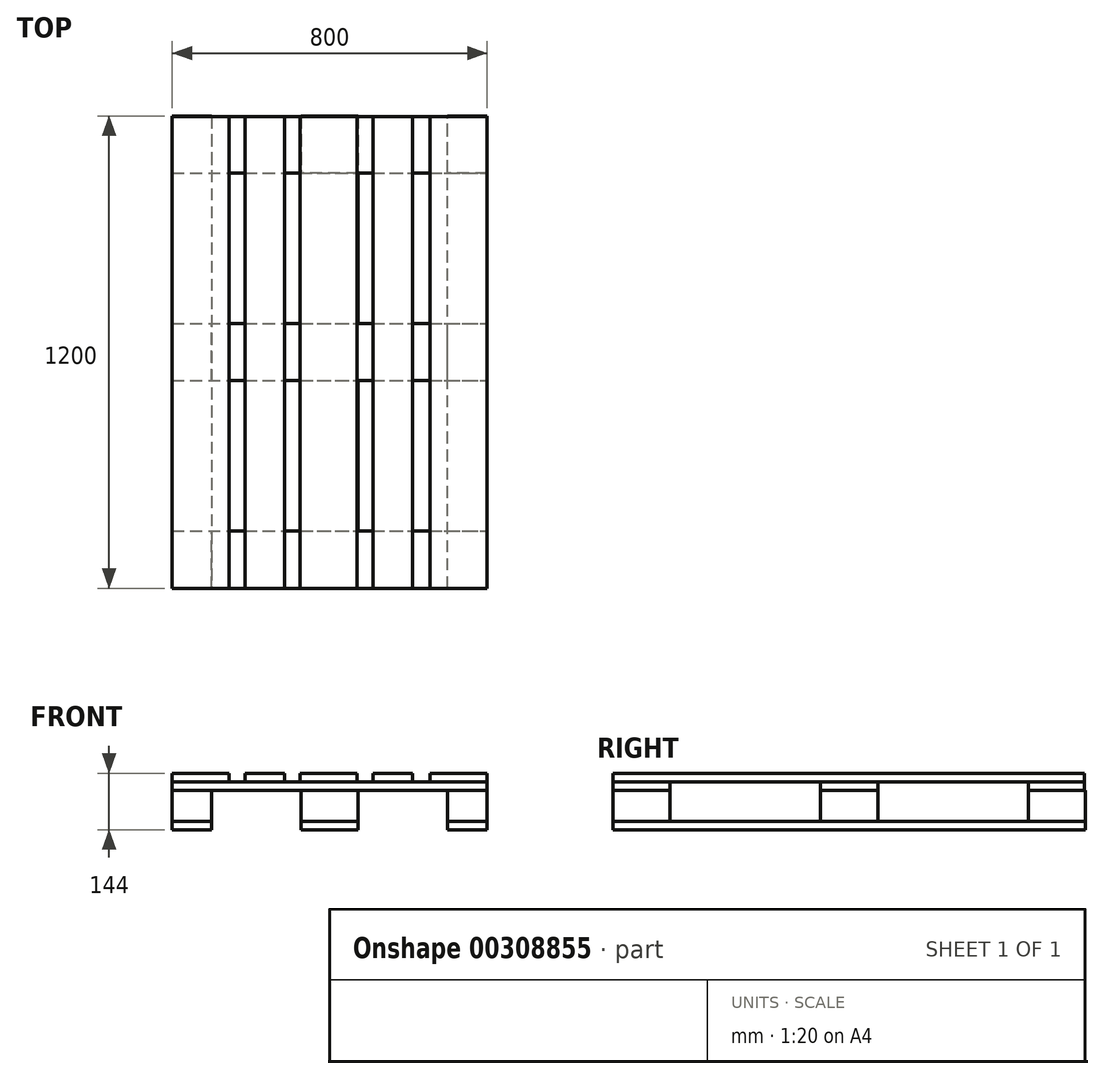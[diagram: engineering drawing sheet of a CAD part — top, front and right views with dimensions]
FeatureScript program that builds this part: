
annotation { "Feature Type Name" : "Feature", "Feature Type Description" : "" }
export const myFeature = defineFeature(function(context is Context, id is Id, definition is map)
    precondition{}
    {
        {
            var Q0;
            Q0=qCreatedBy(makeId("Top.planeOp"),FACE);
            var sketch = newSketch(context, id + "F0", { "sketchPlane" : qUnion([Q0])});
            skLineSegment(sketch, "E0.bottom", {"start": v(-100, 600) * mm, "end": v(0, 600) * mm});
            skLineSegment(sketch, "E0.top", {"start": v(-100, -600) * mm, "end": v(0, -600) * mm});
            skLineSegment(sketch, "E0.left", {"start": v(-100, 600) * mm, "end": v(-100, -600) * mm});
            skLineSegment(sketch, "E0.right", {"start": v(0, 600) * mm, "end": v(0, -600) * mm});
            skLineSegment(sketch, "E1.bottom", {"start": v(227.5, -600) * mm, "end": v(372.5, -600) * mm});
            skLineSegment(sketch, "E1.top", {"start": v(227.5, 600) * mm, "end": v(372.5, 600) * mm});
            skLineSegment(sketch, "E1.left", {"start": v(227.5, -600) * mm, "end": v(227.5, 600) * mm});
            skLineSegment(sketch, "E1.right", {"start": v(372.5, -600) * mm, "end": v(372.5, 600) * mm});
            skPoint(sketch, "E2", {"position": v(300, -600) * mm});
            skLineSegment(sketch, "E3.bottom", {"start": v(600, -600) * mm, "end": v(700, -600) * mm});
            skLineSegment(sketch, "E3.top", {"start": v(600, 600) * mm, "end": v(700, 600) * mm});
            skLineSegment(sketch, "E3.left", {"start": v(600, -600) * mm, "end": v(600, 600) * mm});
            skLineSegment(sketch, "E3.right", {"start": v(700, -600) * mm, "end": v(700, 600) * mm});
            skSolve(sketch);
        }
        {
            var Q0;
            Q0=qSketchRegion(id+"F0",true);
            extrude(context, id + "F1", {"entities" : qUnion([Q0]), "depth" : 22 * mm});
        }
        {
            var Q0;
            Q0=makeQuery(id+"F1.opExtrude","CAP_FACE",FACE,{"disambiguationData":[OSD([sQuery(id+"F0.wireOp",EDGE,"E3.bottom"),sQuery(id+"F0.wireOp",EDGE,"E3.top"),sQuery(id+"F0.wireOp",EDGE,"E3.left"),sQuery(id+"F0.wireOp",EDGE,"E3.right")])],"isStart":false});
            var sketch = newSketch(context, id + "F2", { "sketchPlane" : qUnion([Q0])});
            skLineSegment(sketch, "E4.bottom", {"start": v(-100, -600) * mm, "end": v(0, -600) * mm});
            skLineSegment(sketch, "E4.top", {"start": v(-100, -455) * mm, "end": v(0, -455) * mm});
            skLineSegment(sketch, "E4.left", {"start": v(-100, -600) * mm, "end": v(-100, -455) * mm});
            skLineSegment(sketch, "E4.right", {"start": v(0, -600) * mm, "end": v(0, -455) * mm});
            skLineSegment(sketch, "E5.bottom", {"start": v(227.5, -600) * mm, "end": v(372.5, -600) * mm});
            skLineSegment(sketch, "E5.top", {"start": v(227.5, -455) * mm, "end": v(372.5, -455) * mm});
            skLineSegment(sketch, "E5.left", {"start": v(227.5, -600) * mm, "end": v(227.5, -455) * mm});
            skLineSegment(sketch, "E5.right", {"start": v(372.5, -600) * mm, "end": v(372.5, -455) * mm});
            skLineSegment(sketch, "E6.bottom", {"start": v(600, -600) * mm, "end": v(700, -600) * mm});
            skLineSegment(sketch, "E6.top", {"start": v(600, -455) * mm, "end": v(700, -455) * mm});
            skLineSegment(sketch, "E6.left", {"start": v(600, -600) * mm, "end": v(600, -455) * mm});
            skLineSegment(sketch, "E6.right", {"start": v(700, -600) * mm, "end": v(700, -455) * mm});
            skLineSegment(sketch, "E7.bottom", {"start": v(700, 600) * mm, "end": v(600, 600) * mm});
            skLineSegment(sketch, "E7.top", {"start": v(700, 455) * mm, "end": v(600, 455) * mm});
            skLineSegment(sketch, "E7.left", {"start": v(700, 600) * mm, "end": v(700, 455) * mm});
            skLineSegment(sketch, "E7.right", {"start": v(600, 600) * mm, "end": v(600, 455) * mm});
            skLineSegment(sketch, "E8.bottom", {"start": v(372.5, 600) * mm, "end": v(227.5, 600) * mm});
            skLineSegment(sketch, "E8.top", {"start": v(372.5, 455) * mm, "end": v(227.5, 455) * mm});
            skLineSegment(sketch, "E8.left", {"start": v(372.5, 600) * mm, "end": v(372.5, 455) * mm});
            skLineSegment(sketch, "E8.right", {"start": v(227.5, 600) * mm, "end": v(227.5, 455) * mm});
            skLineSegment(sketch, "E9.bottom", {"start": v(-100, 600) * mm, "end": v(0, 600) * mm});
            skLineSegment(sketch, "E9.top", {"start": v(-100, 455) * mm, "end": v(0, 455) * mm});
            skLineSegment(sketch, "E9.left", {"start": v(-100, 600) * mm, "end": v(-100, 455) * mm});
            skLineSegment(sketch, "E9.right", {"start": v(0, 600) * mm, "end": v(0, 455) * mm});
            skLineSegment(sketch, "E10.bottom", {"start": v(-100, -72.5) * mm, "end": v(0, -72.5) * mm});
            skLineSegment(sketch, "E10.top", {"start": v(-100, 72.5) * mm, "end": v(0, 72.5) * mm});
            skLineSegment(sketch, "E10.left", {"start": v(-100, -72.5) * mm, "end": v(-100, 72.5) * mm});
            skLineSegment(sketch, "E10.right", {"start": v(0, -72.5) * mm, "end": v(0, 72.5) * mm});
            skLineSegment(sketch, "E11.bottom", {"start": v(227.5, -72.5) * mm, "end": v(372.5, -72.5) * mm});
            skLineSegment(sketch, "E11.top", {"start": v(227.5, 72.5) * mm, "end": v(372.5, 72.5) * mm});
            skLineSegment(sketch, "E11.left", {"start": v(227.5, -72.5) * mm, "end": v(227.5, 72.5) * mm});
            skLineSegment(sketch, "E11.right", {"start": v(372.5, -72.5) * mm, "end": v(372.5, 72.5) * mm});
            skLineSegment(sketch, "E12.bottom", {"start": v(600, -72.5) * mm, "end": v(700, -72.5) * mm});
            skLineSegment(sketch, "E12.top", {"start": v(600, 72.5) * mm, "end": v(700, 72.5) * mm});
            skLineSegment(sketch, "E12.left", {"start": v(600, -72.5) * mm, "end": v(600, 72.5) * mm});
            skLineSegment(sketch, "E12.right", {"start": v(700, -72.5) * mm, "end": v(700, 72.5) * mm});
            skSolve(sketch);
        }
        {
            var Q0;
            Q0=makeQuery(id+"F2.imprint","IMPRINT",FACE,{"disambiguationData":[TD([[makeQuery(id+"F2.imprint","IMPRINT",EDGE,{"derivedFrom":sQuery(id+"F2.wireOp",EDGE,"E4.bottom")}),1.0]])]});
            var Q1;
            Q1=makeQuery(id+"F2.imprint","IMPRINT",FACE,{"disambiguationData":[TD([[makeQuery(id+"F2.imprint","IMPRINT",EDGE,{"derivedFrom":sQuery(id+"F2.wireOp",EDGE,"E5.bottom")}),1.0]])]});
            var Q2;
            Q2=makeQuery(id+"F2.imprint","IMPRINT",FACE,{"disambiguationData":[TD([[makeQuery(id+"F2.imprint","IMPRINT",EDGE,{"derivedFrom":sQuery(id+"F2.wireOp",EDGE,"E6.bottom")}),1.0]])]});
            var Q3;
            Q3=makeQuery(id+"F2.imprint","IMPRINT",FACE,{"disambiguationData":[TD([[makeQuery(id+"F2.imprint","IMPRINT",EDGE,{"derivedFrom":sQuery(id+"F2.wireOp",EDGE,"E7.bottom")}),1.0]])]});
            var Q4;
            Q4=makeQuery(id+"F2.imprint","IMPRINT",FACE,{"disambiguationData":[TD([[makeQuery(id+"F2.imprint","IMPRINT",EDGE,{"derivedFrom":sQuery(id+"F2.wireOp",EDGE,"E8.bottom")}),1.0]])]});
            var Q5;
            Q5=makeQuery(id+"F2.imprint","IMPRINT",FACE,{"disambiguationData":[TD([[makeQuery(id+"F2.imprint","IMPRINT",EDGE,{"derivedFrom":sQuery(id+"F2.wireOp",EDGE,"E9.bottom")}),-1.0]])]});
            var Q6;
            Q6=makeQuery(id+"F2.imprint","IMPRINT",FACE,{"disambiguationData":[TD([[makeQuery(id+"F2.imprint","IMPRINT",EDGE,{"derivedFrom":sQuery(id+"F2.wireOp",EDGE,"E10.bottom")}),1.0]])]});
            var Q7;
            Q7=makeQuery(id+"F2.imprint","IMPRINT",FACE,{"disambiguationData":[TD([[makeQuery(id+"F2.imprint","IMPRINT",EDGE,{"derivedFrom":sQuery(id+"F2.wireOp",EDGE,"E11.bottom")}),1.0]])]});
            var Q8;
            Q8=makeQuery(id+"F2.imprint","IMPRINT",FACE,{"disambiguationData":[TD([[makeQuery(id+"F2.imprint","IMPRINT",EDGE,{"derivedFrom":sQuery(id+"F2.wireOp",EDGE,"E12.bottom")}),1.0]])]});
            var Q9;
            Q9=makeQuery(id+"F2.imprint","IMPRINT",FACE,{"disambiguationData":[TD([[makeQuery(id+"F2.imprint","IMPRINT",EDGE,{"derivedFrom":sQuery(id+"F2.wireOp",EDGE,"E7.bottom")}),-1.0]])]});
            extrude(context, id + "F3", {"entities" : qUnion([Q0, Q1, Q2, Q3, Q4, Q5, Q6, Q7, Q8, Q9]), "depth" : 78 * mm});
        }
        {
            var Q0;
            Q0=makeQuery(id+"F3.opExtrude","CAP_FACE",FACE,{"disambiguationData":[OSD([sQuery(id+"F2.wireOp",EDGE,"E9.bottom"),sQuery(id+"F2.wireOp",EDGE,"E9.top"),sQuery(id+"F2.wireOp",EDGE,"E9.left"),sQuery(id+"F2.wireOp",EDGE,"E9.right")])],"isStart":false});
            var sketch = newSketch(context, id + "F4", { "sketchPlane" : qUnion([Q0])});
            skLineSegment(sketch, "E13.bottom", {"start": v(-100, -600) * mm, "end": v(700, -600) * mm});
            skLineSegment(sketch, "E13.top", {"start": v(-100, -455) * mm, "end": v(700, -455) * mm});
            skLineSegment(sketch, "E13.left", {"start": v(-100, -600) * mm, "end": v(-100, -455) * mm});
            skLineSegment(sketch, "E13.right", {"start": v(700, -600) * mm, "end": v(700, -455) * mm});
            skLineSegment(sketch, "E14.bottom", {"start": v(-100, -72.5) * mm, "end": v(700, -72.5) * mm});
            skLineSegment(sketch, "E14.top", {"start": v(-100, 72.5) * mm, "end": v(700, 72.5) * mm});
            skLineSegment(sketch, "E14.left", {"start": v(-100, -72.5) * mm, "end": v(-100, 72.5) * mm});
            skLineSegment(sketch, "E14.right", {"start": v(700, -72.5) * mm, "end": v(700, 72.5) * mm});
            skLineSegment(sketch, "E15.bottom", {"start": v(-100, 455) * mm, "end": v(700, 455) * mm});
            skLineSegment(sketch, "E15.top", {"start": v(-100, 597.77) * mm, "end": v(700, 597.77) * mm});
            skLineSegment(sketch, "E15.left", {"start": v(-100, 455) * mm, "end": v(-100, 597.77) * mm});
            skLineSegment(sketch, "E15.right", {"start": v(700, 455) * mm, "end": v(700, 597.77) * mm});
            skSolve(sketch);
        }
        {
            var Q0;
            Q0=makeQuery(id+"F4.imprint","IMPRINT",FACE,{"disambiguationData":[TD([[makeQuery(id+"F4.imprint","IMPRINT",EDGE,{"derivedFrom":sQuery(id+"F4.wireOp",EDGE,"E13.bottom")}),1.0]])]});
            var Q1;
            Q1=makeQuery(id+"F4.imprint","IMPRINT",FACE,{"disambiguationData":[TD([[makeQuery(id+"F4.imprint","IMPRINT",EDGE,{"derivedFrom":sQuery(id+"F4.wireOp",EDGE,"E14.bottom")}),1.0]])]});
            var Q2;
            {var subQ5=sQuery(id+"F4.wireOp",EDGE,"E15.left");Q2=makeQuery(id+"F4.imprint","IMPRINT",FACE,{"disambiguationData":[TD([[makeQuery(id+"F4.imprint","IMPRINT",EDGE,{"derivedFrom":subQ5}),1.0]])]});}
            var Q3;
            {var subQ5=sQuery(id+"F4.wireOp",EDGE,"E15.right");Q3=makeQuery(id+"F4.imprint","IMPRINT",FACE,{"disambiguationData":[TD([[makeQuery(id+"F4.imprint","IMPRINT",EDGE,{"derivedFrom":subQ5}),1.0]])]});}
            extrude(context, id + "F5", {"entities" : qUnion([Q0, Q1, Q2, Q3]), "depth" : 22 * mm});
        }
        {
            var Q0;
            Q0=makeQuery(id+"F5.opExtrude","CAP_FACE",FACE,{"disambiguationData":[OSD([sQuery(id+"F4.wireOp",EDGE,"E13.bottom"),sQuery(id+"F4.wireOp",EDGE,"E13.top"),sQuery(id+"F4.wireOp",EDGE,"E13.left"),sQuery(id+"F4.wireOp",EDGE,"E13.right")])],"isStart":false});
            var sketch = newSketch(context, id + "F6", { "sketchPlane" : qUnion([Q0])});
            skLineSegment(sketch, "E16.bottom", {"start": v(-100, -600) * mm, "end": v(45, -600) * mm});
            skLineSegment(sketch, "E16.top", {"start": v(-100, 597.77) * mm, "end": v(45, 597.77) * mm});
            skLineSegment(sketch, "E16.left", {"start": v(-100, -600) * mm, "end": v(-100, 597.77) * mm});
            skLineSegment(sketch, "E16.right", {"start": v(45, -600) * mm, "end": v(45, 597.77) * mm});
            skLineSegment(sketch, "E17.bottom", {"start": v(700, 597.77) * mm, "end": v(555, 597.77) * mm});
            skLineSegment(sketch, "E17.top", {"start": v(700, -600) * mm, "end": v(555, -600) * mm});
            skLineSegment(sketch, "E17.left", {"start": v(700, 597.77) * mm, "end": v(700, -600) * mm});
            skLineSegment(sketch, "E17.right", {"start": v(555, 597.77) * mm, "end": v(555, -600) * mm});
            skLineSegment(sketch, "E18.bottom", {"start": v(510, -600) * mm, "end": v(410, -600) * mm});
            skLineSegment(sketch, "E18.top", {"start": v(510, 597.77) * mm, "end": v(410, 597.77) * mm});
            skLineSegment(sketch, "E18.left", {"start": v(510, -600) * mm, "end": v(510, 597.77) * mm});
            skLineSegment(sketch, "E18.right", {"start": v(410, -600) * mm, "end": v(410, 597.77) * mm});
            skLineSegment(sketch, "E19.bottom", {"start": v(370, -600) * mm, "end": v(225, -600) * mm});
            skLineSegment(sketch, "E19.top", {"start": v(370, 597.77) * mm, "end": v(225, 597.77) * mm});
            skLineSegment(sketch, "E19.left", {"start": v(370, -600) * mm, "end": v(370, 597.77) * mm});
            skLineSegment(sketch, "E19.right", {"start": v(225, -600) * mm, "end": v(225, 597.77) * mm});
            skLineSegment(sketch, "E20.bottom", {"start": v(185, -600) * mm, "end": v(85, -600) * mm});
            skLineSegment(sketch, "E20.top", {"start": v(185, 597.77) * mm, "end": v(85, 597.77) * mm});
            skLineSegment(sketch, "E20.left", {"start": v(185, -600) * mm, "end": v(185, 597.77) * mm});
            skLineSegment(sketch, "E20.right", {"start": v(85, -600) * mm, "end": v(85, 597.77) * mm});
            skSolve(sketch);
        }
        {
            var Q0;
            {var subQ5=sQuery(id+"F6.wireOp",EDGE,"E16.bottom");Q0=makeQuery(id+"F6.imprint","IMPRINT",FACE,{"disambiguationData":[TD([[makeQuery(id+"F6.imprint","IMPRINT",EDGE,{"derivedFrom":subQ5}),1.0]])]});}
            var Q1;
            {var subQ5=sQuery(id+"F6.wireOp",EDGE,"E16.top");Q1=makeQuery(id+"F6.imprint","IMPRINT",FACE,{"disambiguationData":[TD([[makeQuery(id+"F6.imprint","IMPRINT",EDGE,{"derivedFrom":subQ5}),-1.0]])]});}
            var Q2;
            {var subQ6=sQuery(id+"F6.wireOp",EDGE,"E20.bottom");Q2=makeQuery(id+"F6.imprint","IMPRINT",FACE,{"disambiguationData":[TD([[makeQuery(id+"F6.imprint","IMPRINT",EDGE,{"derivedFrom":subQ6}),1.0]])]});}
            var Q3;
            {var subQ5=sQuery(id+"F6.wireOp",EDGE,"E20.top");Q3=makeQuery(id+"F6.imprint","IMPRINT",FACE,{"disambiguationData":[TD([[makeQuery(id+"F6.imprint","IMPRINT",EDGE,{"derivedFrom":subQ5}),1.0]])]});}
            var Q4;
            {var subQ6=sQuery(id+"F6.wireOp",EDGE,"E19.bottom");Q4=makeQuery(id+"F6.imprint","IMPRINT",FACE,{"disambiguationData":[TD([[makeQuery(id+"F6.imprint","IMPRINT",EDGE,{"derivedFrom":subQ6}),1.0]])]});}
            var Q5;
            {var subQ5=sQuery(id+"F6.wireOp",EDGE,"E19.top");Q5=makeQuery(id+"F6.imprint","IMPRINT",FACE,{"disambiguationData":[TD([[makeQuery(id+"F6.imprint","IMPRINT",EDGE,{"derivedFrom":subQ5}),1.0]])]});}
            var Q6;
            {var subQ5=sQuery(id+"F6.wireOp",EDGE,"E18.top");Q6=makeQuery(id+"F6.imprint","IMPRINT",FACE,{"disambiguationData":[TD([[makeQuery(id+"F6.imprint","IMPRINT",EDGE,{"derivedFrom":subQ5}),1.0]])]});}
            var Q7;
            {var subQ5=sQuery(id+"F6.wireOp",EDGE,"E17.top");Q7=makeQuery(id+"F6.imprint","IMPRINT",FACE,{"disambiguationData":[TD([[makeQuery(id+"F6.imprint","IMPRINT",EDGE,{"derivedFrom":subQ5}),1.0]])]});}
            var Q8;
            {var subQ5=sQuery(id+"F6.wireOp",EDGE,"E17.bottom");Q8=makeQuery(id+"F6.imprint","IMPRINT",FACE,{"disambiguationData":[TD([[makeQuery(id+"F6.imprint","IMPRINT",EDGE,{"derivedFrom":subQ5}),1.0]])]});}
            var Q9;
            {var subQ6=sQuery(id+"F6.wireOp",EDGE,"E18.bottom");Q9=makeQuery(id+"F6.imprint","IMPRINT",FACE,{"disambiguationData":[TD([[makeQuery(id+"F6.imprint","IMPRINT",EDGE,{"derivedFrom":subQ6}),1.0]])]});}
            extrude(context, id + "F7", {"entities" : qUnion([Q0, Q1, Q2, Q3, Q4, Q5, Q6, Q7, Q8, Q9]), "depth" : 22 * mm});
        }
    });
